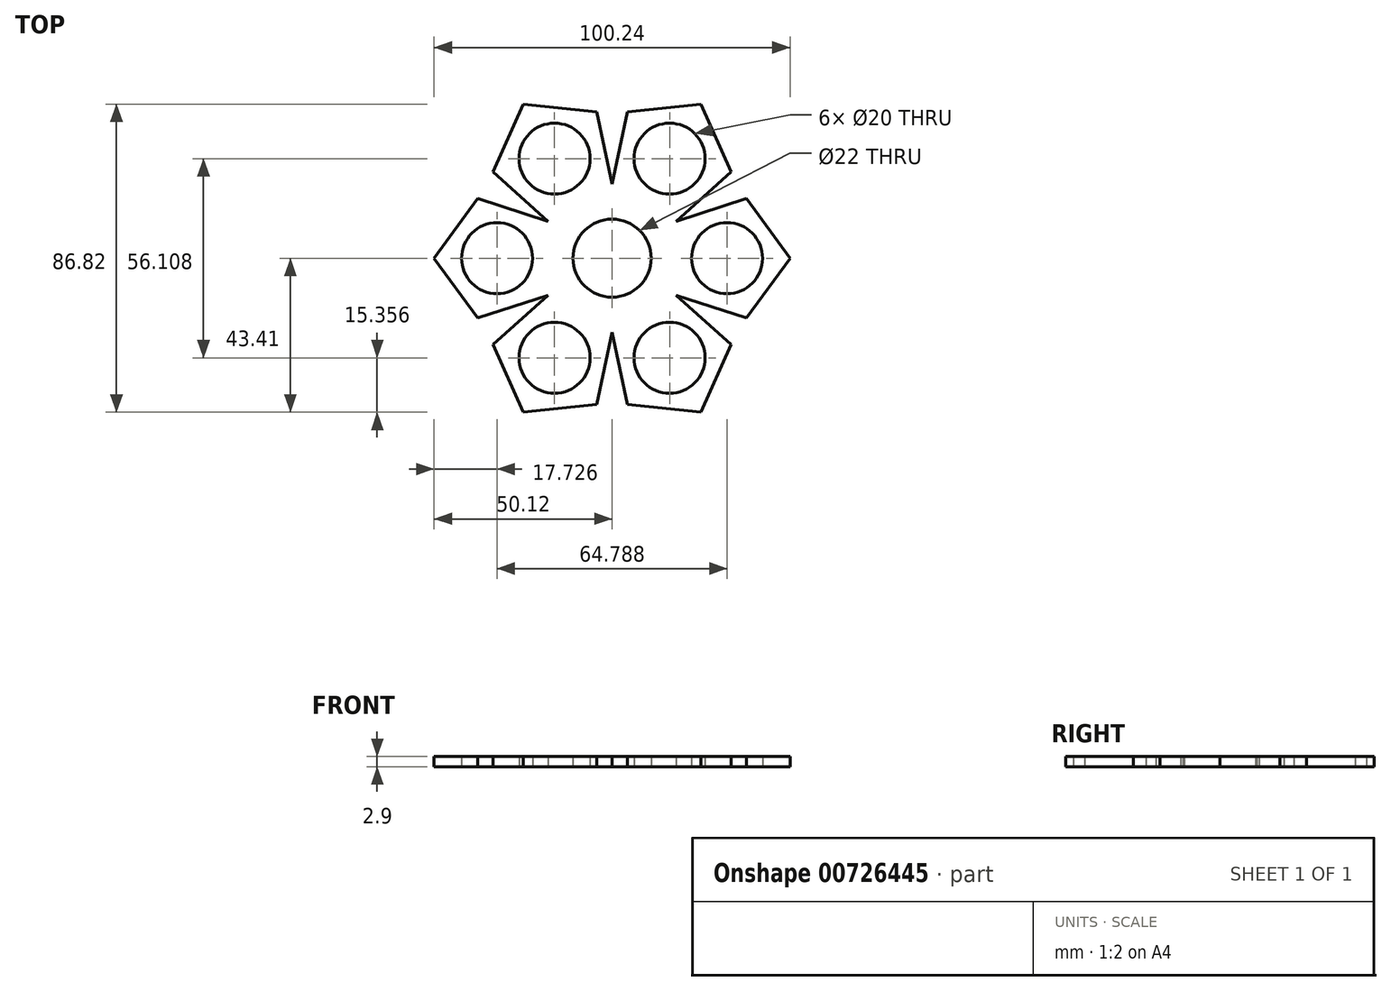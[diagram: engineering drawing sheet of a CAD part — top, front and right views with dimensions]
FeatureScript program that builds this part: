
annotation { "Feature Type Name" : "Feature", "Feature Type Description" : "" }
export const myFeature = defineFeature(function(context is Context, id is Id, definition is map)
    precondition{}
    {
        {
            var Q0;
            Q0=qCreatedBy(makeId("Top.planeOp"),FACE);
            var sketch = newSketch(context, id + "F0", { "sketchPlane" : qUnion([Q0])});
            skLineSegment(sketch, "E0", {"start": v(0, 0) * mm, "end": v(0, 70.1) * mm});
            skLineSegment(sketch, "E1", {"start": v(0, 0) * mm, "end": v(0, -74.5) * mm});
            skLineSegment(sketch, "E2", {"start": v(0, 0) * mm, "end": v(-74.04, 0) * mm});
            skLineSegment(sketch, "E3", {"start": v(0, 0) * mm, "end": v(74.35, 0) * mm});
            skPoint(sketch, "E4.0.midPoint", {"position": v(9.03, -15.63) * mm});
            skLineSegment(sketch, "E5.0", {"start": v(33.54, 24.37) * mm, "end": v(18.05, 10.42) * mm});
            skLineSegment(sketch, "E5.2", {"start": v(0, 20.84) * mm, "end": v(4.33, 41.23) * mm});
            skLineSegment(sketch, "E5.3", {"start": v(4.33, 41.23) * mm, "end": v(25.06, 43.4) * mm});
            skLineSegment(sketch, "E5.4", {"start": v(25.06, 43.4) * mm, "end": v(33.54, 24.37) * mm});
            skPoint(sketch, "E5.0.midPoint", {"position": v(25.8, 17.4) * mm});
            skPoint(sketch, "E6", {"position": v(0, 20.84) * mm});
            skPoint(sketch, "E7", {"position": v(-120.57, 65.7) * mm});
            skCircle(sketch, "E8", {"center": v(0, 0) * mm, "radius": 11 * mm});
            skLineSegment(sketch, "E9.1", {"start": v(-18.05, 10.42) * mm, "end": v(-33.54, 24.37) * mm});
            skLineSegment(sketch, "E9.2", {"start": v(-33.54, 24.37) * mm, "end": v(-25.06, 43.4) * mm});
            skLineSegment(sketch, "E9.3", {"start": v(-25.06, 43.4) * mm, "end": v(-4.33, 41.23) * mm});
            skLineSegment(sketch, "E9.4", {"start": v(-4.33, 41.23) * mm, "end": v(0, 20.84) * mm});
            skPoint(sketch, "E9.0.midPoint", {"position": v(-9.03, 15.63) * mm});
            skPoint(sketch, "E10", {"position": v(-33.54, 24.37) * mm});
            skLineSegment(sketch, "E11.0", {"start": v(-18.05, -10.42) * mm, "end": v(-37.87, -16.86) * mm});
            skLineSegment(sketch, "E11.1", {"start": v(-37.87, -16.86) * mm, "end": v(-50.12, 0) * mm});
            skLineSegment(sketch, "E11.2", {"start": v(-50.12, 0) * mm, "end": v(-37.87, 16.86) * mm});
            skLineSegment(sketch, "E11.3", {"start": v(-37.87, 16.86) * mm, "end": v(-18.05, 10.42) * mm});
            skPoint(sketch, "E11.0.midPoint", {"position": v(-27.96, -13.64) * mm});
            skPoint(sketch, "E12", {"position": v(-50.12, 0) * mm});
            skLineSegment(sketch, "E13.0", {"start": v(50.12, 0) * mm, "end": v(37.87, -16.86) * mm});
            skLineSegment(sketch, "E13.1", {"start": v(37.87, -16.86) * mm, "end": v(18.05, -10.42) * mm});
            skLineSegment(sketch, "E13.3", {"start": v(18.05, 10.42) * mm, "end": v(37.87, 16.86) * mm});
            skLineSegment(sketch, "E13.4", {"start": v(37.87, 16.86) * mm, "end": v(50.12, 0) * mm});
            skPoint(sketch, "E13.0.midPoint", {"position": v(44, -8.43) * mm});
            skPoint(sketch, "E14", {"position": v(18.05, -10.42) * mm});
            skLineSegment(sketch, "E15.0", {"start": v(25.06, -43.4) * mm, "end": v(4.33, -41.23) * mm});
            skLineSegment(sketch, "E15.1", {"start": v(4.33, -41.23) * mm, "end": v(0, -20.84) * mm});
            skLineSegment(sketch, "E15.3", {"start": v(18.05, -10.42) * mm, "end": v(33.54, -24.37) * mm});
            skLineSegment(sketch, "E15.4", {"start": v(33.54, -24.37) * mm, "end": v(25.06, -43.4) * mm});
            skPoint(sketch, "E15.0.midPoint", {"position": v(14.7, -42.32) * mm});
            skPoint(sketch, "E16", {"position": v(0, -20.84) * mm});
            skLineSegment(sketch, "E17.0", {"start": v(-4.33, -41.23) * mm, "end": v(-25.06, -43.4) * mm});
            skLineSegment(sketch, "E17.1", {"start": v(-25.06, -43.4) * mm, "end": v(-33.54, -24.37) * mm});
            skLineSegment(sketch, "E17.2", {"start": v(-33.54, -24.37) * mm, "end": v(-18.05, -10.42) * mm});
            skLineSegment(sketch, "E17.4", {"start": v(0, -20.84) * mm, "end": v(-4.33, -41.23) * mm});
            skPoint(sketch, "E17.0.midPoint", {"position": v(-14.7, -42.32) * mm});
            skPoint(sketch, "E18", {"position": v(-33.54, -24.37) * mm});
            skCircle(sketch, "E19", {"center": v(-16.2, 28.05) * mm, "radius": 10 * mm});
            skCircle(sketch, "E20", {"center": v(16.2, 28.05) * mm, "radius": 10 * mm});
            skCircle(sketch, "E21", {"center": v(32.4, 0) * mm, "radius": 10 * mm});
            skCircle(sketch, "E22", {"center": v(16.2, -28.05) * mm, "radius": 10 * mm});
            skCircle(sketch, "E23", {"center": v(-16.2, -28.05) * mm, "radius": 10 * mm});
            skCircle(sketch, "E24", {"center": v(-32.4, 0) * mm, "radius": 10 * mm});
            skPoint(sketch, "E25.orphan", {"position": v(16.2, -25.36) * mm});
            skSolve(sketch);
        }
        {
            var Q0;
            Q0 = qSketchRegion(id + "F0", true);
            extrude(context, id + "F1", {"entities" : qUnion([Q0]), "depth" : 2.9 * mm, "offsetDistance" : 25 * mm});
        }
    });
